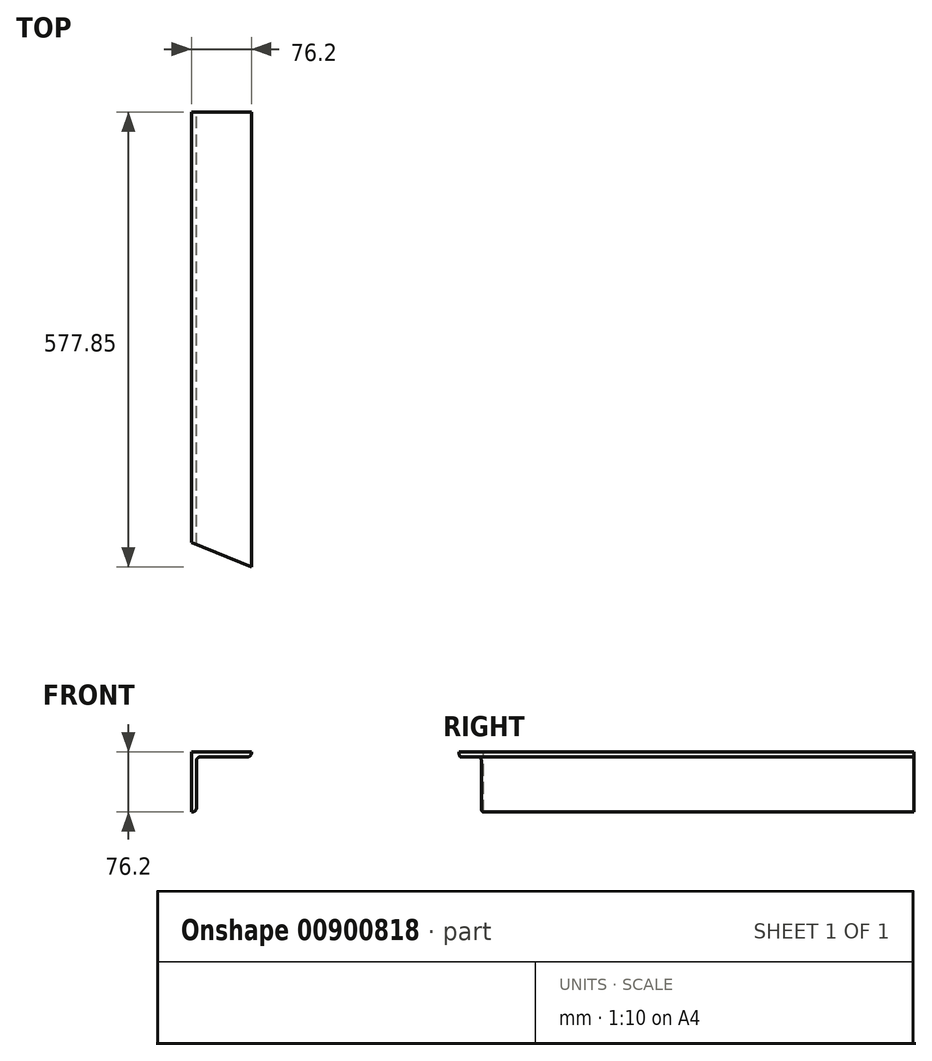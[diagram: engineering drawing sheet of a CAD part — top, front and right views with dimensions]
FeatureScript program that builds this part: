
annotation { "Feature Type Name" : "Feature", "Feature Type Description" : "" }
export const myFeature = defineFeature(function(context is Context, id is Id, definition is map)
    precondition{}
    {
        {
            var Q0;
            Q0=qCreatedBy(makeId("Front.planeOp"),FACE);
            var sketch = newSketch(context, id + "F0", { "sketchPlane" : qUnion([Q0])});
            skLineSegment(sketch, "E0.bottom", {"start": v(-31.75, -38.1) * mm, "end": v(-38.1, -38.1) * mm});
            skLineSegment(sketch, "E0.top", {"start": v(38.1, 38.1) * mm, "end": v(-38.1, 38.1) * mm});
            skLineSegment(sketch, "E0.left", {"start": v(38.1, 31.75) * mm, "end": v(38.1, 38.1) * mm});
            skLineSegment(sketch, "E0.right", {"start": v(-38.1, -38.1) * mm, "end": v(-38.1, 38.1) * mm});
            skPoint(sketch, "E0.middle", {"position": v(0, 0) * mm});
            skLineSegment(sketch, "E1.0", {"start": v(38.1, 31.75) * mm, "end": v(-31.75, 31.75) * mm});
            skLineSegment(sketch, "E2.0", {"start": v(-31.75, -38.1) * mm, "end": v(-31.75, 31.75) * mm});
            skPoint(sketch, "E3.orphan", {"position": v(38.1, -38.1) * mm});
            skSolve(sketch);
        }
        {
            var Q0;
            Q0 = qSketchRegion(id + "F0", true);
            extrude(context, id + "F1", {"entities" : qUnion([Q0]), "depth" : 577.85 * mm, "offsetDistance" : 25.4 * mm});
        }
        {
            var Q0;
            Q0=makeQuery(id+"F1.opExtrude","SWEPT_EDGE",EDGE,{"disambiguationData":[OSD([sQuery(id+"F0.wireOp",EDGE,"E1.0"),sQuery(id+"F0.wireOp",EDGE,"E2.0")])]});
            var Q1;
            Q1=makeQuery(id+"F1.opExtrude","SWEPT_EDGE",EDGE,{"disambiguationData":[OSD([sQuery(id+"F0.wireOp",EDGE,"E0.left"),sQuery(id+"F0.wireOp",EDGE,"E1.0")])]});
            var Q2;
            Q2=makeQuery(id+"F1.opExtrude","SWEPT_EDGE",EDGE,{"disambiguationData":[OSD([sQuery(id+"F0.wireOp",EDGE,"E0.bottom"),sQuery(id+"F0.wireOp",EDGE,"E2.0")])]});
            fillet(context, id + "F2", {"entities" : qUnion([Q0, Q1, Q2]), "radius" : 5.08 * mm, "tangentPropagation" : true, "allowEdgeOverflow" : false});
        }
        {
            var Q0;
            Q0=makeQuery(id+"F1.opExtrude","SWEPT_FACE",FACE,{"disambiguationData":[OSD([sQuery(id+"F0.wireOp",EDGE,"E0.top")])]});
            var sketch = newSketch(context, id + "F3", { "sketchPlane" : qUnion([Q0])});
            skPoint(sketch, "E4.0", {"position": v(-38.1, -577.85) * mm});
            skPoint(sketch, "E5.0", {"position": v(38.1, -577.85) * mm});
            skLineSegment(sketch, "E6", {"start": v(38.1, -577.85) * mm, "end": v(-38.1, -547.06) * mm});
            skLineSegment(sketch, "E7", {"start": v(-38.1, -547.06) * mm, "end": v(-38.1, -577.85) * mm});
            skSolve(sketch);
        }
        {
            var Q0;
            Q0=makeQuery(id+"F3.imprint","IMPRINT",FACE,{"disambiguationData":[TD([[makeQuery(id+"F3.imprint","IMPRINT",EDGE,{"derivedFrom":sQuery(id+"F3.wireOp",EDGE,"E6")}),1.0]])]});
            extrude(context, id + "F4", {"entities" : qUnion([Q0]), "operationType" : NewBodyOperationType.REMOVE, "oppositeDirection" : true, "depth" : 76.2 * mm, "offsetDistance" : 25.4 * mm});
        }
    });
